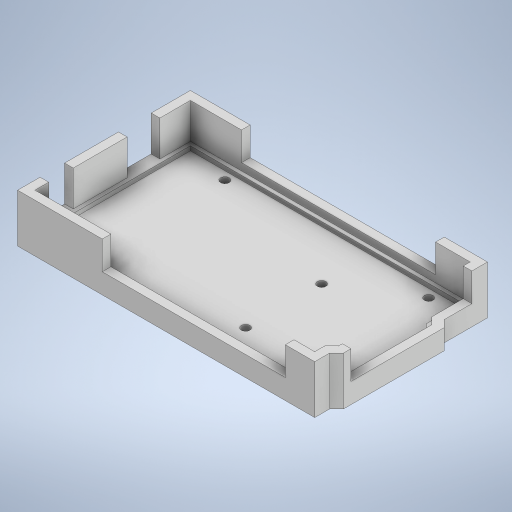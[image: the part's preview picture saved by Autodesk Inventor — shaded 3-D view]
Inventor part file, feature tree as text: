
AUTODESK INVENTOR PART (.ipt)
format: ipt  version: 2024 (Build 280153000, 153)  size: 562,176 bytes
history: native  units: in
note: dims shown in document units (in); Inventor stores cm internally (conversion verified against a paired STEP export)
features: sketch x7, extrude x5, mirror x1
ambient origin geometry x8: Origin, YZ Plane, XZ Plane, XY Plane, X Axis, Y Axis, Z Axis, Center Point
bodies: Solid1 (feature_tree)
feature tree (13):
  sketch  "Sketch1"  dims[d0=2.1in d1=0.125in]
  extrude  "Extrusion1"  Depth=0.125in
  extrude  "Extrusion2"  Depth=0.3543in
  extrude  "Extrusion3"  Depth=0.25in
  extrude  "Extrusion4"  Depth=0.474in
  mirror  "Mirror1"
  extrude  "Extrusion5"  Depth=0.5382in
  sketch  "Sketch6"  dims[d10=0.1in]
  sketch  "Sketch7"  dims[d11=0.6in d12=0.1in d13=0.35in d14=0.1in d15=0.1in d16=0.1in d17=0.7in d18=1.3in d19=1.3in d20=0.3in d21=0.51in d22=0.1in d23=0.1in d24=0.1in d25=0.1in d26=0.1in d27=0.125in d28=0.125in d29=0.125in d30=0.125in d31=0.125in d32=0.125in d33=0.2in d34=0.125in d35=0.2in d36=0.125in d37=2.1in d38=0.125in d39=0.075in d40=0.3543in d41=0.3661in d42=0.25in d43=0.474in d44=3.9in d45=3.9in d46=0.5382in d47=0.1in d48=0.6in d49=0.1in d50=0.35in d51=0.1in d52=0.1in d53=0.1in d54=0.7in d55=1.3in d56=1.3in d57=0.3in d58=0.51in d59=0.1in d60=0.1in d61=0.1in d62=0.1in d63=0.1in d64=0.125in d65=0.125in d66=0.125in d67=0.125in d68=0.125in d69=0.125in d70=0.2in d71=0.125in d72=0.2in d73=0.125in d74=2.1in d75=0.125in d76=0.075in d77=0.3543in d78=0.3661in d79=0.25in d80=0.474in d81=3.9in d82=3.9in d83=0.5382in d84=0.1in d85=0.6in d86=0.1in d87=0.35in d88=0.1in d89=0.1in d90=0.1in d91=0.7in d92=1.3in d93=1.3in d94=0.3in d95=0.51in d96=0.1in d97=0.1in d98=0.1in d99=0.1in d100=0.1in d101=0.125in d102=0.125in d103=0.125in d104=0.125in d105=0.125in d106=0.125in d107=0.2in d108=0.125in d109=0.2in d110=0.125in d111=2.1in d112=0.125in d113=0.075in d114=0.3543in d115=0.3661in d116=0.25in d117=0.474in d118=3.9in d119=3.9in d120=0.5382in d121=0.1in d122=0.6in d123=0.1in d124=0.35in d125=0.1in d126=0.1in d127=0.1in d128=0.7in d129=1.3in d130=1.3in d131=0.3in d132=0.51in d133=0.1in d134=0.1in d135=0.1in d136=0.1in d137=0.1in d138=0.125in d139=0.125in d140=0.125in d141=0.125in d142=0.125in d143=0.125in d144=0.2in d145=0.125in d146=0.2in d147=0.125in d148=2.1in d149=0.125in d150=0.075in d151=0.3543in d152=0.3661in d153=0.25in d154=0.474in d155=3.9in d156=3.9in d157=0.5382in d158=0.1in d159=0.6in d160=0.1in d161=0.35in d162=0.1in d163=0.1in d164=0.1in d165=0.7in d166=1.3in d167=1.3in d168=0.3in d169=0.51in d170=0.1in d171=0.1in d172=0.1in d173=0.1in d174=0.1in d175=0.125in d176=0.125in d177=0.125in d178=0.125in d179=0.125in d180=0.125in d181=0.2in d182=0.125in d183=0.2in d184=0.125in d185=0.125in d186=0.0in d187=0.0625in d188=0.0in d189=0.5756in d190=0.0in d191=0.75in d192=0.0in d193=1.225in d194=2.65in d195=0.865in d196=2.81in d197=0.225in d198=1.85in d199=0.41in d200=0.0in]
  sketch  "Sketch2"  dims[d2=0.075in d3=0.3543in]
  sketch  "Sketch3"  dims[d4=0.3661in d5=0.25in]
  sketch  "Sketch4"  dims[d6=0.474in d7=3.9in]
  sketch  "Sketch5"  dims[d8=3.9in d9=0.5382in]
